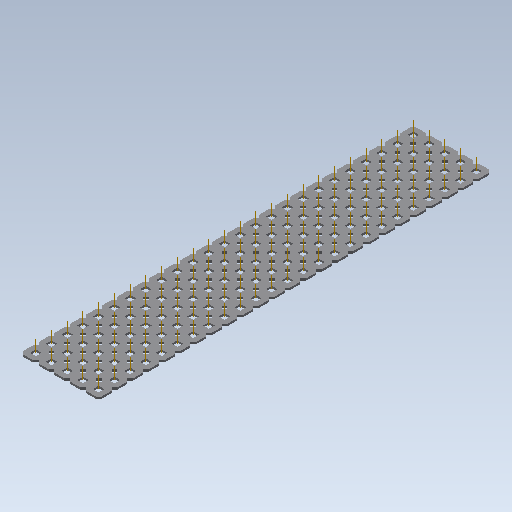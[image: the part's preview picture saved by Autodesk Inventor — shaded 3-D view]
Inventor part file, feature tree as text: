
AUTODESK INVENTOR PART (.ipt)
format: ipt  version: 2020 (Build 240168000, 168)  size: 1,347,584 bytes
history: native  units: in
note: dims shown in document units (in); Inventor stores cm internally (conversion verified against a paired STEP export)
features: other x134, extrude x2, pattern_linear x1, imported_body x1
ambient origin geometry x8: Origin, YZ Plane, XZ Plane, XY Plane, X Axis, Y Axis, Z Axis, Center Point
bodies: Body1 (feature_tree)
feature tree (138):
  other  "Diamond-Pattern"
  other  "Plate"
  extrude  "length cut"  TaperAngle=0.0deg  [1 undecoded]
  extrude  "width cut"  TaperAngle=0.0deg  [1 undecoded]
  other  "constraint axis"
  pattern_linear  "constraint axes"  Spacing1=0.5in  [1 undecoded]
  other  "front plane"
  other  "right plane"
  imported_body  "Base1"
  other  "length profile"
  other  "width profile"
  other  "Work Point1"
  other  "Work Axis36"
  other  "Work Axis37"
  other  "Work Axis38"
  other  "Work Axis39"
  other  "Work Axis40"
  other  "Work Axis41"
  other  "Work Axis42"
  other  "Work Axis43"
  other  "Work Axis44"
  other  "Work Axis45"
  other  "Work Axis46"
  other  "Work Axis47"
  other  "Work Axis48"
  other  "Work Axis49"
  other  "Work Axis50"
  other  "Work Axis51"
  other  "Work Axis52"
  other  "Work Axis53"
  other  "Work Axis54"
  other  "Work Axis55"
  other  "Work Axis56"
  other  "Work Axis57"
  other  "Work Axis58"
  other  "Work Axis59"
  other  "Work Axis60"
  other  "Work Axis61"
  other  "Work Axis62"
  other  "Work Axis63"
  other  "Work Axis64"
  other  "back plane"
  other  "left plane"
  other  "Work Axis75"
  other  "Work Axis76"
  other  "Work Axis77"
  other  "Work Axis78"
  other  "Work Axis79"
  other  "Work Axis80"
  other  "Work Axis81"
  other  "Work Axis82"
  other  "Work Axis83"
  other  "Work Axis84"
  other  "Work Axis85"
  other  "Work Axis86"
  other  "Work Axis87"
  other  "Work Axis88"
  other  "Work Axis89"
  other  "Work Axis90"
  other  "Work Axis91"
  other  "Work Axis92"
  other  "Work Axis93"
  other  "Work Axis94"
  other  "Work Axis95"
  other  "Work Axis96"
  other  "Work Axis97"
  other  "Work Axis98"
  other  "Work Axis99"
  other  "Work Axis100"
  other  "Work Axis101"
  other  "Work Axis102"
  other  "Work Axis103"
  other  "Work Axis104"
  other  "Work Axis105"
  other  "Work Axis106"
  other  "Work Axis107"
  other  "Work Axis108"
  other  "Work Axis109"
  other  "Work Axis110"
  other  "Work Axis111"
  other  "Work Axis112"
  other  "Work Axis113"
  other  "Work Axis114"
  other  "Work Axis115"
  other  "Work Axis116"
  other  "Work Axis117"
  other  "Work Axis118"
  other  "Work Axis119"
  other  "Work Axis120"
  other  "Work Axis121"
  other  "Work Axis122"
  other  "Work Axis123"
  other  "Work Axis124"
  other  "Work Axis125"
  other  "Work Axis126"
  other  "Work Axis127"
  other  "Work Axis128"
  other  "Work Axis129"
  other  "Work Axis130"
  other  "Work Axis131"
  other  "Work Axis132"
  other  "Work Axis133"
  other  "Work Axis134"
  other  "Work Axis135"
  other  "Work Axis136"
  other  "Work Axis137"
  other  "Work Axis138"
  other  "Work Axis139"
  other  "Work Axis140"
  other  "Work Axis141"
  other  "Work Axis142"
  other  "Work Axis143"
  other  "Work Axis144"
  other  "Work Axis145"
  other  "Work Axis146"
  other  "Work Axis147"
  other  "Work Axis148"
  other  "Work Axis149"
  other  "Work Axis150"
  other  "Work Axis151"
  other  "Work Axis152"
  other  "Work Axis153"
  other  "Work Axis154"
  other  "Work Axis155"
  other  "Work Axis156"
  other  "Work Axis157"
  other  "Work Axis158"
  other  "Work Axis159"
  other  "Work Axis160"
  other  "Work Axis161"
  other  "Work Axis162"
  other  "Work Axis163"
  other  "Work Axis164"
  other  "Work Axis165"
  other  "Work Axis166"
  other  "Work Axis167"
  other  "Work Axis168"
  other  "Work Axis169"
note: 3 required parameter values undecoded (feature->parameter linkage not recoverable at this tier; creation-order binding heuristic only, values carry confidence <= 0.55)
